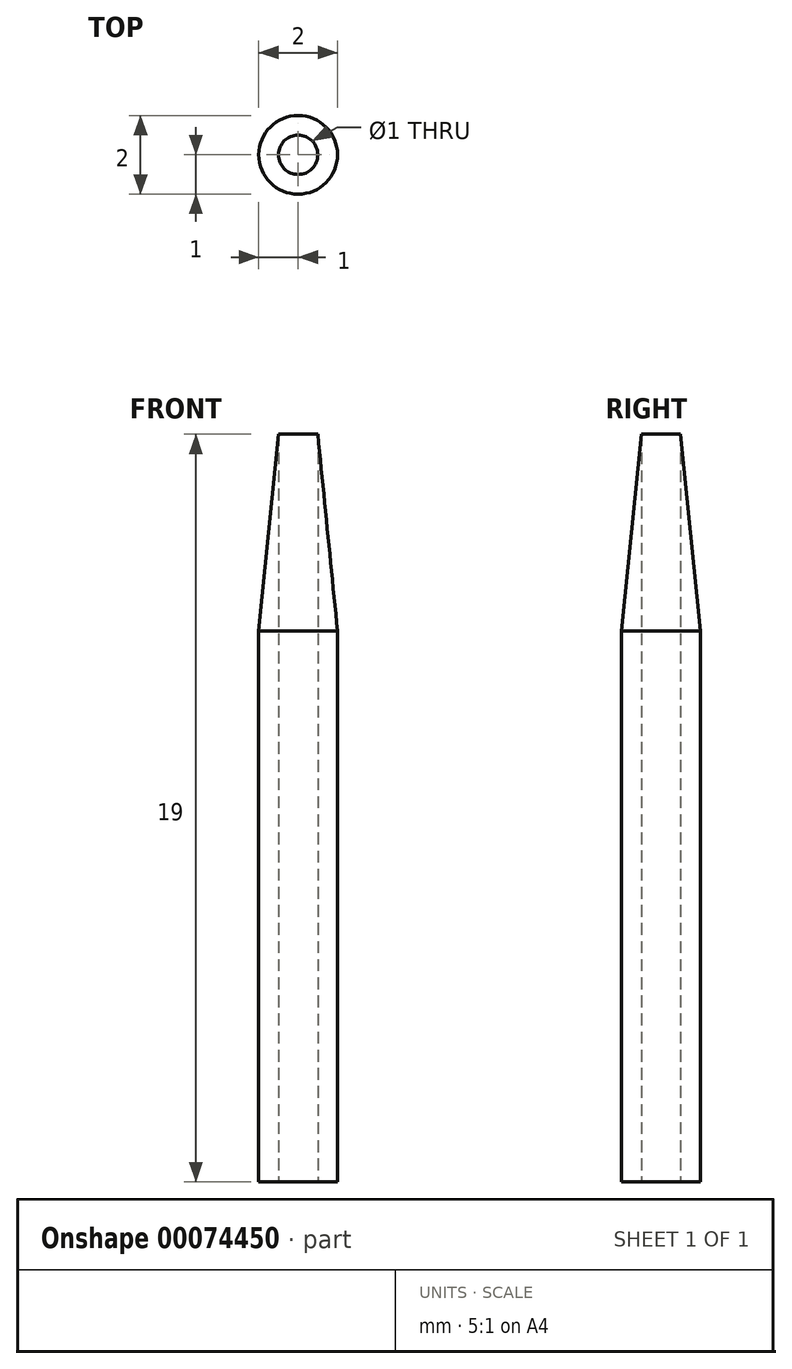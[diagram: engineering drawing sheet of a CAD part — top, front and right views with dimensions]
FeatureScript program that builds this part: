
annotation { "Feature Type Name" : "Feature", "Feature Type Description" : "" }
export const myFeature = defineFeature(function(context is Context, id is Id, definition is map)
    precondition{}
    {
        {
            var Q0;
            Q0=qCreatedBy(makeId("Top.planeOp"),FACE);
            var sketch = newSketch(context, id + "F0", { "sketchPlane" : qUnion([Q0])});
            skCircle(sketch, "E0", {"center": v(0, 0) * mm, "radius": 1 * mm});
            skCircle(sketch, "E1", {"center": v(0, 0) * mm, "radius": 0.5 * mm});
            skSolve(sketch);
        }
        {
            var Q0;
            Q0=makeQuery(id+"F0.imprint","IMPRINT",FACE,{"disambiguationData":[TD([[makeQuery(id+"F0.imprint","IMPRINT",EDGE,{"derivedFrom":sQuery(id+"F0.wireOp",EDGE,"E0")}),1.0]])]});
            extrude(context, id + "F1", {"entities" : qUnion([Q0]), "depth" : 19 * mm});
        }
        {
            var Q0;
            Q0=makeQuery(id+"F1.opExtrude","CAP_EDGE",EDGE,{"disambiguationData":[OSD([sQuery(id+"F0.wireOp",EDGE,"E0")])],"isStart":false});
            chamfer(context, id + "F2", {"entities" : qUnion([Q0]), "chamferType" : ChamferType.TWO_OFFSETS, "width1" : 0.5 * mm, "oppositeDirection" : false, "width2" : 5 * mm, "tangentPropagation" : true});
        }
    });
